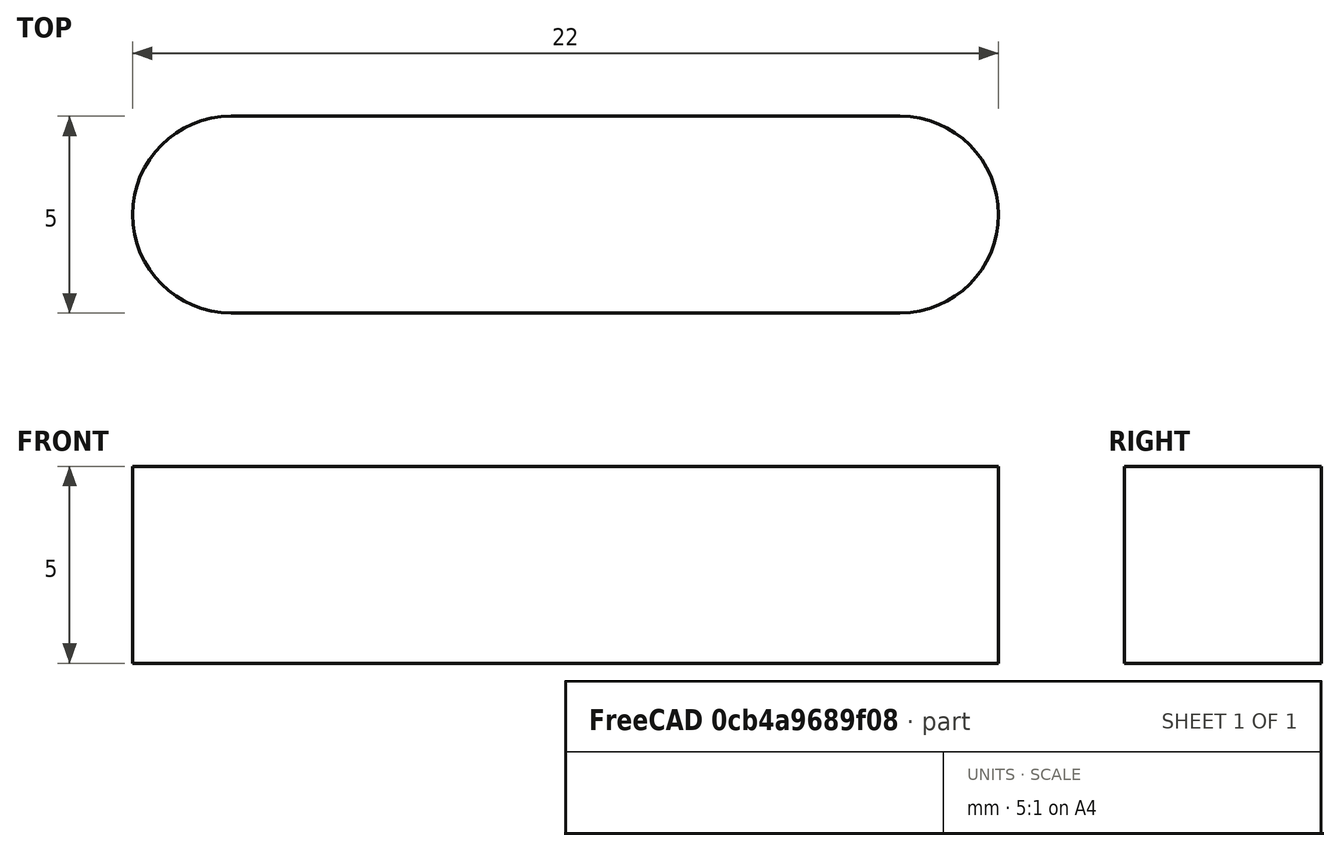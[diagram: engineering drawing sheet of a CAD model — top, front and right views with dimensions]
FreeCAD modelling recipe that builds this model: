
FCSTD DOCUMENT  (FreeCAD 0.20R29126 (Git))
Label: electric-motor-parallel-key
License: All rights reserved
LicenseURL: http://en.wikipedia.org/wiki/All_rights_reserved
objects: Sketcher::SketchObject×1, PartDesign::Pad×1, PartDesign::Body×1
note: 4 computed .brp shape members not serialized (recipe doc carries the construction recipe); baked Part::Feature solids carry a one-line shape summary decoded from their .brp

FEATURE [Sketcher::SketchObject] Sketch
  FullyConstrained = true
  MapMode = 5
  Support = -> [XY_Plane]
  sketch-geometry (4):
    g0: ArcOfCircle CenterX=0 CenterY=0 CenterZ=0 NormalX=0 NormalY=0 NormalZ=1 AngleXU=0 Radius=2.5 StartAngle=1.5708 EndAngle=4.71239
    g1: ArcOfCircle CenterX=17 CenterY=0 CenterZ=0 NormalX=0 NormalY=0 NormalZ=1 AngleXU=0 Radius=2.5 StartAngle=4.71239 EndAngle=7.85398
    g2: LineSegment StartX=-7.3079e-12 StartY=-2.5 StartZ=0 EndX=17 EndY=-2.5 EndZ=0
    g3: LineSegment StartX=17 StartY=2.5 StartZ=0 EndX=-7.3079e-12 EndY=2.5 EndZ=0
  constraints (9):
    c: Tangent(g0,g2) = -1.5708
    c: Tangent(g2,g1) = -1.5708
    c: Tangent(g1,g3) = -1.5708
    c: Tangent(g3,g0) = -1.5708
    c: Equal(g0,g1)
    c: PointOnObject(g1,g-1)
    c: DistanceY(g1,g1) = 5
    c: DistanceX(g0,g1) = 17
    c: Coincident(g0,g-1)
FEATURE [PartDesign::Pad] Pad
  Direction = (0,0,1)
  Length = 5
  Length2 = 10
  Profile = -> Sketch
  ReferenceAxis = -> Sketch [N_Axis]
  Type = 0
FEATURE [PartDesign::Body] Body
  Group = -> [Sketch,Pad]
  Origin = -> Origin
  Tip = -> Pad
